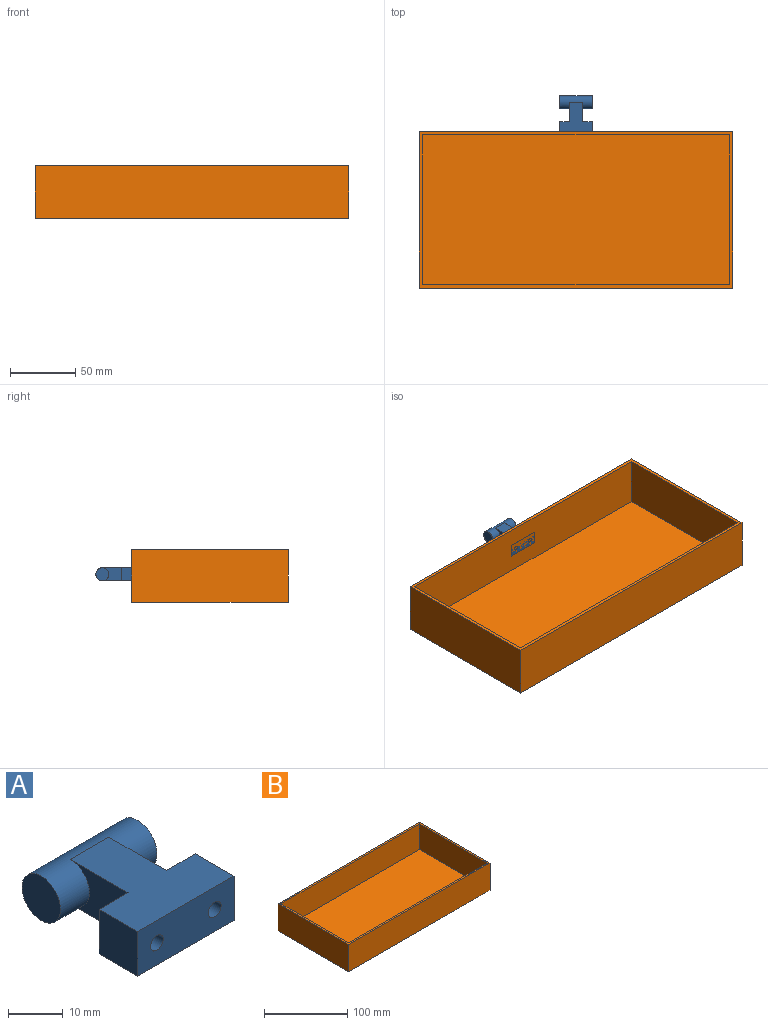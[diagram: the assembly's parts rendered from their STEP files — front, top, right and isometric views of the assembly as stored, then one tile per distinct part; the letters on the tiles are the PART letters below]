
ASSEMBLY  parts=2 mates=1
PART A: 14 faces, bbox 25x30x10 mm
  f0: cylinder r=5mm len=25mm, axis (1,0,0), area 628.3mm2, adj f1,f2,f3,f9,f10,f11
  f1: plane 10x10mm, normal (-1,0,0), area 78.5mm2, adj f0
  f2: plane 10x10mm, normal (1,0,0), area 78.5mm2, adj f0
  f3: plane 15x10mm, normal (-1,0,0), area 110.7mm2, adj f0,f4,f10,f11
  f4: plane 10x7.5mm, normal (0,1,0), area 66.4mm2, adj f3,f5,f10,f11,f12
  f5: plane 10x10mm, normal (-1,0,0), area 100mm2, adj f4,f6,f10,f11
  f6: plane 25x10mm, normal (0,-1,0), area 232.9mm2, adj f5,f7,f10,f11,f12,f13
  f7: plane 10x10mm, normal (1,0,0), area 100mm2, adj f6,f8,f10,f11
  f8: plane 10x7.5mm, normal (0,1,0), area 66.4mm2, adj f7,f9,f10,f11,f13
  f9: plane 15x10mm, normal (1,0,0), area 110.7mm2, adj f0,f8,f10,f11
  f10: plane 25x25mm, normal (0,0,1), area 400mm2, adj f0,f3,f4,f5,f6,f7,f8,f9
  f11: plane 25x25mm, normal (0,0,-1), area 400mm2, adj f0,f3,f4,f5,f6,f7,f8,f9
  f12: cylinder r=1.65mm len=10mm, axis (0,-1,0), area 103.7mm2, adj f4,f6
  f13: cylinder r=1.65mm len=10mm, axis (0,-1,0), area 103.7mm2, adj f6,f8
PART B: 11 faces, bbox 240x120x40 mm
  f0: plane 120x40mm, normal (-1,0,0), area 4800mm2, adj f1,f3,f4,f5
  f1: plane 240x40mm, normal (0,-1,0), area 9600mm2, adj f0,f2,f4,f5
  f2: plane 120x40mm, normal (1,0,0), area 4800mm2, adj f1,f3,f4,f5
  f3: plane 240x40mm, normal (0,1,0), area 9600mm2, adj f0,f2,f4,f5
  f4: plane 240x120mm, normal (0,0,1), area 1775mm2, adj f0,f1,f2,f3,f6,f7,f8,f9
  f5: plane 240x120mm, normal (0,0,-1), area 28800mm2, adj f0,f1,f2,f3
  f6: plane 115x37.5mm, normal (1,0,0), area 4312.5mm2, adj f4,f7,f9,f10
  f7: plane 235x37.5mm, normal (0,1,0), area 8812.5mm2, adj f4,f6,f8,f10
  f8: plane 115x37.5mm, normal (-1,0,0), area 4312.5mm2, adj f4,f7,f9,f10
  f9: plane 235x37.5mm, normal (0,-1,0), area 8812.5mm2, adj f4,f6,f8,f10
  f10: plane 235x115mm, normal (0,0,1), area 27025mm2, adj f6,f7,f8,f9
PLACE A at identity
PLACE B t=(-132.5,2.5,-16.25)mm
MATE planar B.f9 <-> A.f6  axis (0,-1,0) through (-12.5,0,5)mm
